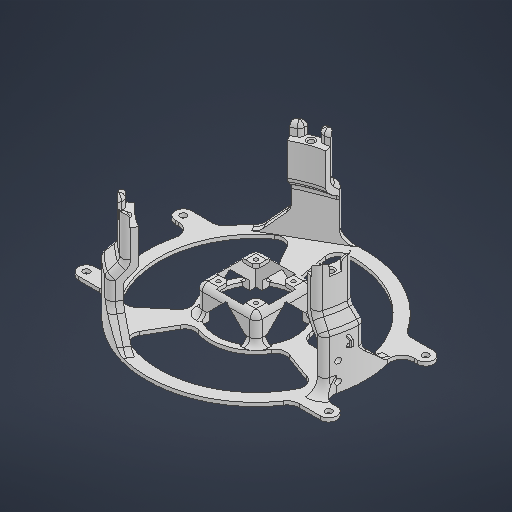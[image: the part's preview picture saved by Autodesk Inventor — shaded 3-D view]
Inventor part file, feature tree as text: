
AUTODESK INVENTOR PART (.ipt)
format: ipt  version: 2025.1 (Build 291241000, 241)  size: 2,070,528 bytes
history: native  units: mm
features: fillet x13, extrude x12, sketch x9, projected_geometry x5, chamfer x4, plane x3, revolve x1, pattern_circular x1
ambient origin geometry x8: Origin, YZ Plane, XZ Plane, XY Plane, X Axis, Y Axis, Z Axis, Center Point
bodies: Solid1 (feature_tree)
feature tree (48):
  sketch  "Sketch1"  dims[d0=43.5mm d1=43.5mm]
  extrude  "Extrusion1"  Depth=43.5mm
  extrude  "Extrusion2"  Depth=3.2mm
  chamfer  "Chamfer5"  Distance=3.0mm
  sketch  "Sketch3"  dims[d4=3.0mm]
  revolve  "Revolution1"  [1 undecoded]
  sketch  "Sketch5"  dims[d5=3.0mm d6=3.0mm d7=0.0mm]
  extrude  "Extrusion7"  Depth=2.0mm
  extrude  "Extrusion12"  Depth=2.0mm
  sketch  "Sketch7"  dims[d8=23.0mm d9=0.0mm d10=35.0mm]
  extrude  "Extrusion11"  Depth=2.0mm
  fillet  "Fillet7"  Radius=2.0mm
  fillet  "Fillet2"  Radius=40.0mm
  extrude  "Extrusion16"  Depth=5.0mm
  extrude  "Extrusion17"  Depth=5.0mm TaperAngle=45.0deg
  extrude  "Extrusion19"  Depth=5.0mm
  fillet  "Fillet4"  Radius=10.0mm
  fillet  "Fillet16"  [1 undecoded]
  fillet  "Fillet17"  Radius=71.0mm
  fillet  "Fillet18"  Radius=40.0mm
  fillet  "Fillet19"  Radius=78.0mm
  pattern_circular  "Circular Pattern1"  [2 undecoded]
  fillet  "Fillet10"  Radius=10.0mm
  fillet  "Fillet11"  Radius=180.0mm
  fillet  "Fillet12"  Radius=75.0mm
  sketch  "Sketch9"  dims[d38=2.0mm d39=2.0mm]
  extrude  "Extrusion14"  Depth=5.0mm
  chamfer  "Chamfer8"  Distance=3.0mm
  fillet  "Fillet13"  Radius=5.0mm
  extrude  "Extrusion15"  Depth=5.0mm
  fillet  "Fillet14"  Radius=4.6mm
  chamfer  "Chamfer10"  Distance=8.0mm
  fillet  "Fillet15"  Radius=5.0mm
  extrude  "Extrusion13"  Depth=5.0mm
  plane  "Work Plane7"
  plane  "Work Plane5"
  plane  "Work Plane8"
  sketch  "Sketch13"  dims[d67=2.0mm d68=2.0mm d71=16.0mm d72=2.0mm d73=45.0deg d74=80.0mm d75=10.0mm d77=45.0deg d78=71.0mm d79=40.0mm d80=78.0mm d81=10.0mm d82=10.0mm d86=180.0mm d87=75.0mm d88=3.490659mm d89=3.0mm d90=0.0mm d91=5.0mm d94=76.0mm d95=4.6mm d96=8.0mm d104=5.0mm d106=5.0mm d107=30.0mm d108=360.0deg d115=0.0mm d116=0.0mm d117=9.0mm d120=3.0mm d121=0.0mm d122=9.0mm d123=5.0mm d124=5.0mm d125=4.5mm d126=4.5mm d127=15.0mm d128=5.0mm d130=6.0mm d131=0.0mm d132=3.0mm d133=3.0mm d134=3.0mm d135=3.0mm d136=1.5mm d137=0.0mm d138=1.5mm d139=2.0mm d140=45.0deg d141=20.0mm d142=4.0mm d144=6.0mm d145=6.0mm d146=4.0mm d147=5.4mm d148=40.0mm d149=100.0mm d150=15.0mm d151=0.0mm d152=10.0mm d156=10.0mm d157=20.0mm d158=2.0mm d159=45.0deg d160=2.8mm d161=20.0mm d162=0.0mm d163=1.0mm d164=152.4mm d165=30.0deg d166=30.0deg d169=7.0mm d170=7.0mm d171=10.0mm d172=0.0mm d173=4.0mm d174=4.0mm d177=20.071286mm d181=30.0mm d182=2.0mm d183=0.0mm d187=20.071286mm d188=2.0mm d189=2.0mm d190=2.0mm d191=2.5mm d193=2.0mm d195=15.0mm d196=1.1mm d197=1.0mm d198=2.0mm d199=45.0deg d200=5.0mm d201=0.0mm d202=1.0mm d203=0.5mm d46=0.5mm d47=0.872665mm d48=0.5mm d49=0.872665mm d50=0.0mm d112=0.0mm d113=0.0mm d114=0.0mm]
  extrude  "Extrusion18"  Depth=5.0mm TaperAngle=360.0deg
  chamfer  "Chamfer12"  [1 undecoded]
  sketch  "Sketch Circular Pattern1"  dims[d2=31.0mm d3=3.2mm]
  projected_geometry  "Projected Loop4"
  projected_geometry  "Projected Loop5"
  sketch  "Sketch8"  dims[d23=22.0mm d37=2.0mm]
  projected_geometry  "Projected Loop6"
  sketch  "Sketch10"  dims[d40=2.0mm d41=2.0mm d42=2.0mm d63=40.0mm d65=360.0deg]
  projected_geometry  "Projected Loop7"
  projected_geometry  "Projected Loop8"
note: 5 required parameter values undecoded (feature->parameter linkage not recoverable at this tier; creation-order binding heuristic only, values carry confidence <= 0.55)